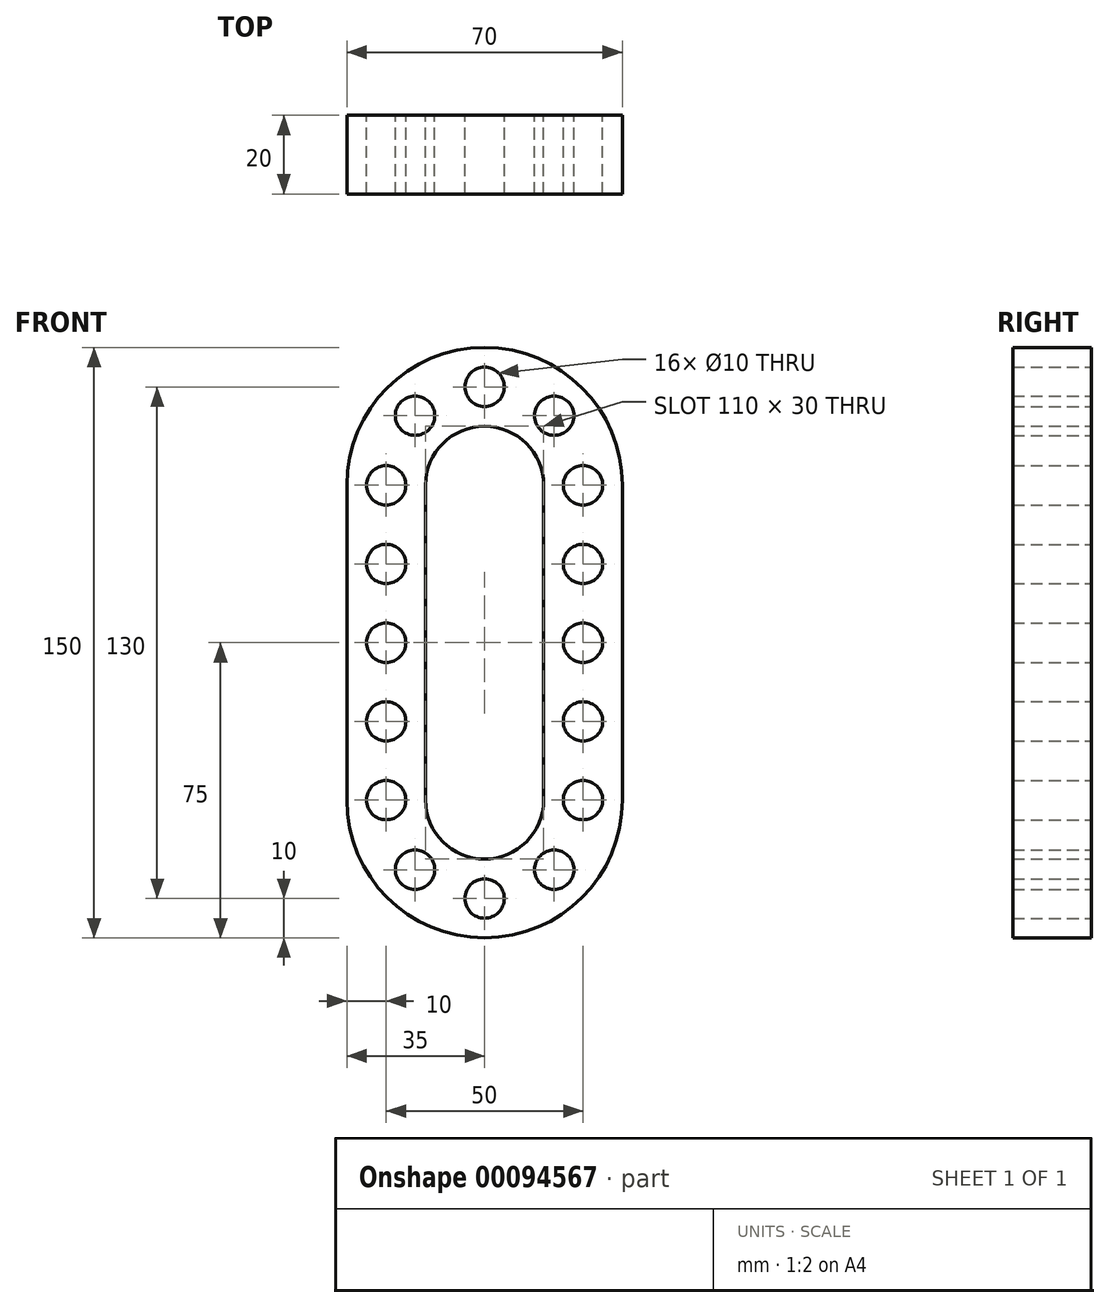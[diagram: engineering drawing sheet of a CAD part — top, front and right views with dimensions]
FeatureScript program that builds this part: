
annotation { "Feature Type Name" : "Feature", "Feature Type Description" : "" }
export const myFeature = defineFeature(function(context is Context, id is Id, definition is map)
    precondition{}
    {
        {
            var Q0;
            Q0=qCreatedBy(makeId("Front.planeOp"),FACE);
            var sketch = newSketch(context, id + "F0", { "sketchPlane" : qUnion([Q0])});
            skPoint(sketch, "E0", {"position": v(-25, 40) * mm});
            skLineSegment(sketch, "E1", {"start": v(-25, 40) * mm, "end": v(-25, 0) * mm, "construction": true});
            skArc(sketch, "E2", {"start": v(0, 65) * mm, "mid": v(-17.68, 57.68) * mm, "end": v(-25, 40) * mm, "construction": true});
            skArc(sketch, "E3.0.startCap", {"start": v(0, 75) * mm, "mid": v(10, 65) * mm, "end": v(0, 55) * mm, "construction": true});
            skArc(sketch, "E3.0.endCap", {"start": v(-15, 40) * mm, "mid": v(-25, 30) * mm, "end": v(-35, 40) * mm, "construction": true});
            skArc(sketch, "E3.0.left", {"start": v(0, 55) * mm, "mid": v(-10.6, 50.6) * mm, "end": v(-15, 40) * mm});
            skArc(sketch, "E3.0.right", {"start": v(0, 75) * mm, "mid": v(-24.75, 64.75) * mm, "end": v(-35, 40) * mm});
            skArc(sketch, "E3.1.startCap", {"start": v(-35, 40) * mm, "mid": v(-25, 50) * mm, "end": v(-15, 40) * mm, "construction": true});
            skArc(sketch, "E3.1.endCap", {"start": v(-15, 0) * mm, "mid": v(-25, -10) * mm, "end": v(-35, 0) * mm, "construction": true});
            skLineSegment(sketch, "E3.1.left", {"start": v(-15, 40) * mm, "end": v(-15, 0) * mm});
            skLineSegment(sketch, "E3.1.right", {"start": v(-35, 40) * mm, "end": v(-35, 0) * mm});
            skCircle(sketch, "E4", {"center": v(-25, 40) * mm, "radius": 5 * mm});
            skCircle(sketch, "E5.0.1.0", {"center": v(-25, 20) * mm, "radius": 5 * mm});
            skCircle(sketch, "E5.0.2.0", {"center": v(-25, 0) * mm, "radius": 5 * mm});
            skLineSegment(sketch, "E5.direction1", {"start": v(-25, 40) * mm, "end": v(0, 40) * mm, "construction": true});
            skLineSegment(sketch, "E5.direction2", {"start": v(-25, 40) * mm, "end": v(-25, 20) * mm, "construction": true});
            skCircle(sketch, "E6.1.0", {"center": v(-17.68, 57.68) * mm, "radius": 5 * mm});
            skCircle(sketch, "E6.2.0", {"center": v(0, 65) * mm, "radius": 5 * mm});
            skLineSegment(sketch, "E6.anchor1", {"start": v(0, 40) * mm, "end": v(-25, 40) * mm, "construction": true});
            skLineSegment(sketch, "E6.anchor2", {"start": v(0, 40) * mm, "end": v(0, 65) * mm, "construction": true});
            skLineSegment(sketch, "E7", {"start": v(0, 75) * mm, "end": v(0, 65) * mm});
            skLineSegment(sketch, "E8", {"start": v(0, 55) * mm, "end": v(0, 65) * mm});
            skLineSegment(sketch, "E9", {"start": v(-25, 0) * mm, "end": v(-35, 0) * mm});
            skLineSegment(sketch, "E10", {"start": v(-25, 0) * mm, "end": v(-15, 0) * mm});
            skSolve(sketch);
        }
        {
            var Q0;
            {var subQ10=sQuery(id+"F0.wireOp",EDGE,"E3.0.left");Q0=makeQuery(id+"F0.imprint","IMPRINT",FACE,{"disambiguationData":[TD([[makeQuery(id+"F0.imprint","IMPRINT",EDGE,{"derivedFrom":subQ10}),-1.0]])]});}
            extrude(context, id + "F1", {"entities" : qUnion([Q0]), "depth" : 20 * mm});
        }
        {
            var Q0;
            Q0=makeQuery(id+"F1.opExtrude","SWEPT_BODY",BODY,{"disambiguationData":[OSD([sQuery(id+"F0.wireOp",EDGE,"E3.0.left"),sQuery(id+"F0.wireOp",EDGE,"E3.0.right"),sQuery(id+"F0.wireOp",EDGE,"E3.1.left"),sQuery(id+"F0.wireOp",EDGE,"E3.1.right"),sQuery(id+"F0.wireOp",EDGE,"E4"),sQuery(id+"F0.wireOp",EDGE,"E5.0.1.0"),sQuery(id+"F0.wireOp",EDGE,"E5.0.2.0"),sQuery(id+"F0.wireOp",EDGE,"E6.1.0"),sQuery(id+"F0.wireOp",EDGE,"E6.2.0"),sQuery(id+"F0.wireOp",EDGE,"E7"),sQuery(id+"F0.wireOp",EDGE,"E8"),sQuery(id+"F0.wireOp",EDGE,"E9"),sQuery(id+"F0.wireOp",EDGE,"E10")])]});
            var Q1;
            Q1=qCreatedBy(makeId("Right.planeOp"),FACE);
            mirror(context, id + "F2", {"operationType" : NewBodyOperationType.ADD, "entities" : qUnion([Q0]), "mirrorPlane" : qUnion([Q1])});
        }
        {
            var Q0;
            Q0=makeQuery(id+"F1.opExtrude","SWEPT_BODY",BODY,{"disambiguationData":[OSD([sQuery(id+"F0.wireOp",EDGE,"E3.0.left"),sQuery(id+"F0.wireOp",EDGE,"E3.0.right"),sQuery(id+"F0.wireOp",EDGE,"E3.1.left"),sQuery(id+"F0.wireOp",EDGE,"E3.1.right"),sQuery(id+"F0.wireOp",EDGE,"E4"),sQuery(id+"F0.wireOp",EDGE,"E5.0.1.0"),sQuery(id+"F0.wireOp",EDGE,"E5.0.2.0"),sQuery(id+"F0.wireOp",EDGE,"E6.1.0"),sQuery(id+"F0.wireOp",EDGE,"E6.2.0"),sQuery(id+"F0.wireOp",EDGE,"E7"),sQuery(id+"F0.wireOp",EDGE,"E8"),sQuery(id+"F0.wireOp",EDGE,"E9"),sQuery(id+"F0.wireOp",EDGE,"E10")])]});
            var Q1;
            Q1=qCreatedBy(makeId("Top.planeOp"),FACE);
            mirror(context, id + "F3", {"operationType" : NewBodyOperationType.ADD, "entities" : qUnion([Q0]), "mirrorPlane" : qUnion([Q1])});
        }
    });
